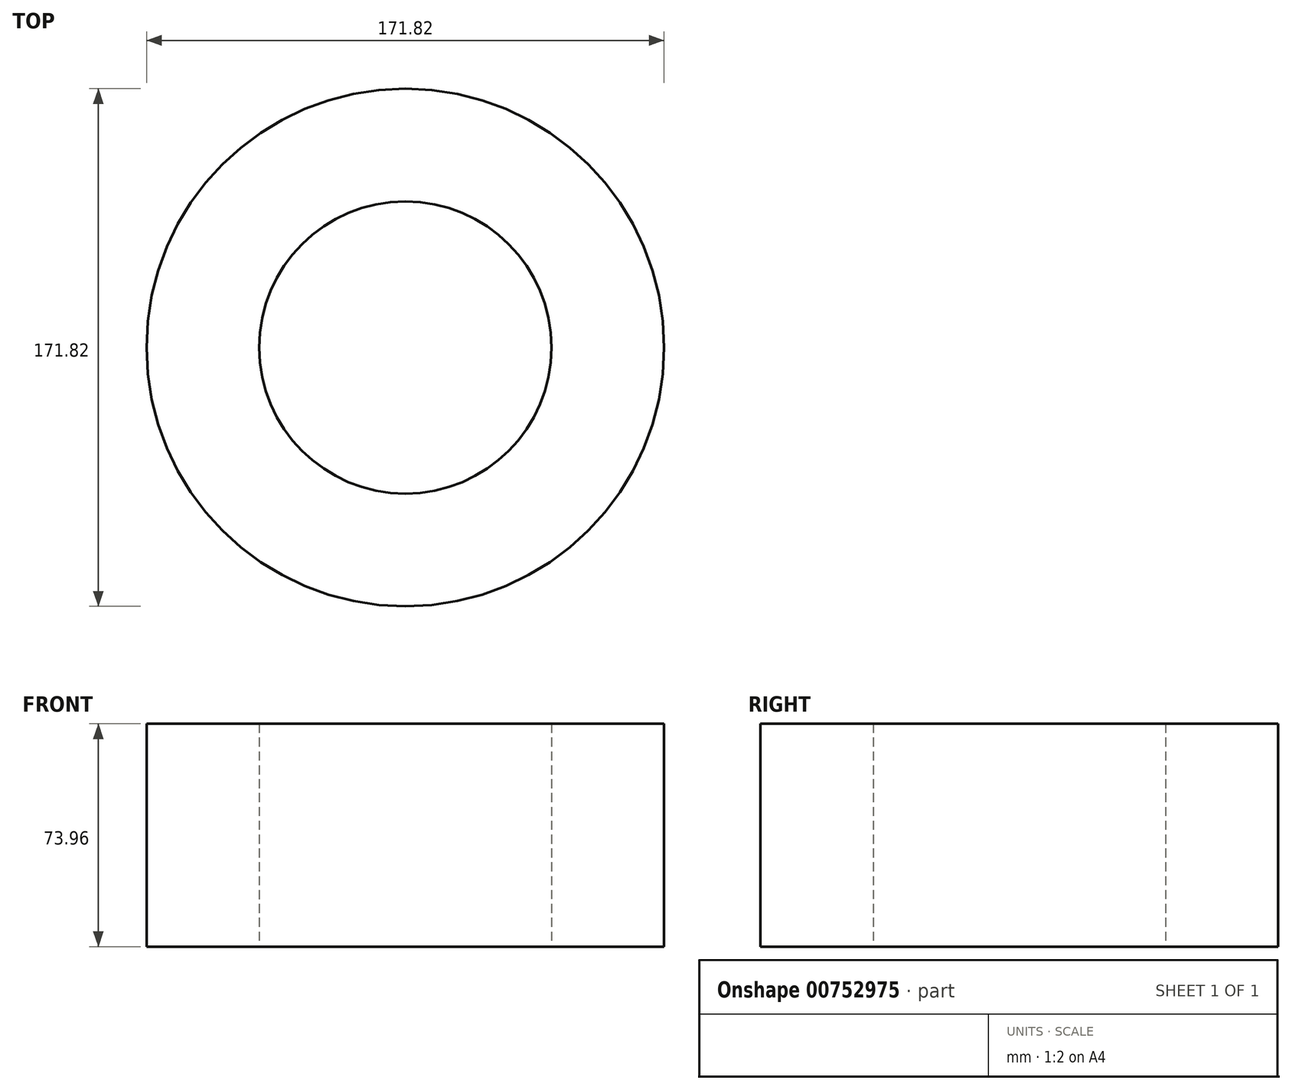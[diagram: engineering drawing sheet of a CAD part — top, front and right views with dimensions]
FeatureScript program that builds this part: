
annotation { "Feature Type Name" : "Feature", "Feature Type Description" : "" }
export const myFeature = defineFeature(function(context is Context, id is Id, definition is map)
    precondition{}
    {
        {
            var Q0;
            Q0=qCreatedBy(makeId("Front.planeOp"),FACE);
            var sketch = newSketch(context, id + "F0", { "sketchPlane" : qUnion([Q0])});
            skLineSegment(sketch, "E0.bottom", {"start": v(85.91, 36.98) * mm, "end": v(48.5, 36.98) * mm});
            skLineSegment(sketch, "E0.top", {"start": v(85.91, -36.98) * mm, "end": v(48.5, -36.98) * mm});
            skLineSegment(sketch, "E0.left", {"start": v(85.91, 36.98) * mm, "end": v(85.91, -36.98) * mm});
            skLineSegment(sketch, "E0.right", {"start": v(48.5, 36.98) * mm, "end": v(48.5, -36.98) * mm});
            skPoint(sketch, "E0.middle", {"position": v(67.2, 0) * mm});
            skLineSegment(sketch, "E1", {"start": v(0, 0) * mm, "end": v(0, 49.07) * mm});
            skSolve(sketch);
        }
        {
            var Q0;
            Q0 = qSketchRegion(id + "F0", true);
            var Q1;
            Q1=sQuery(id+"F0.wireOp",EDGE,"E1");
            revolve(context, id + "F1", {"surfaceOperationType" : NewSurfaceOperationType.NEW, "entities" : qUnion([Q0]), "axis" : qUnion([Q1]), "revolveType" : RevolveType.FULL});
        }
    });
